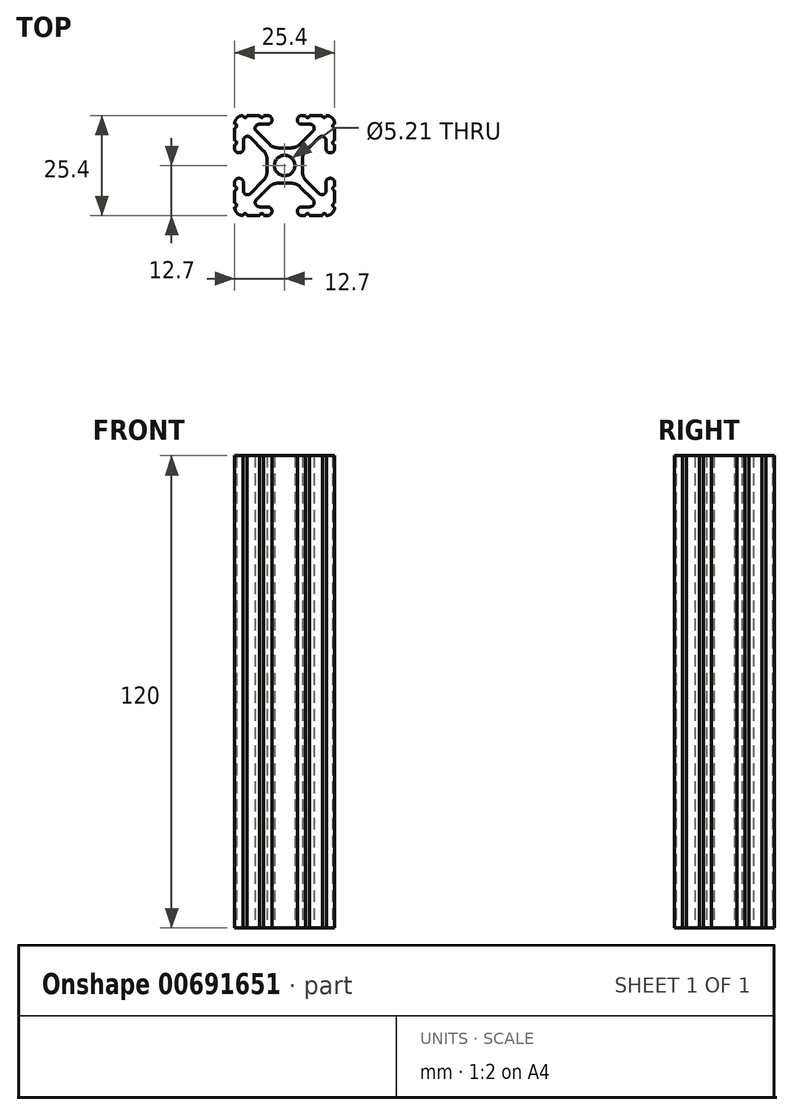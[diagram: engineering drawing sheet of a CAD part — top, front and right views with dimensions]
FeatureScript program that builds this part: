
annotation { "Feature Type Name" : "Feature", "Feature Type Description" : "" }
export const myFeature = defineFeature(function(context is Context, id is Id, definition is map)
    precondition{}
    {
        {
            var Q0;
            Q0=qCreatedBy(makeId("Top.planeOp"),FACE);
            var sketch = newSketch(context, id + "F0", { "sketchPlane" : qUnion([Q0])});
            skCircle(sketch, "E0", {"center": v(0, 0) * mm, "radius": 2.6 * mm});
            skArc(sketch, "E1", {"start": v(-1.7, -4.5) * mm, "mid": v(-2.92, -4.74) * mm, "end": v(-3.95, -5.42) * mm});
            skLineSegment(sketch, "E2", {"start": v(-1.7, -4.5) * mm, "end": v(1.7, -4.5) * mm});
            skArc(sketch, "E3", {"start": v(3.95, -5.42) * mm, "mid": v(2.92, -4.74) * mm, "end": v(1.7, -4.5) * mm});
            skLineSegment(sketch, "E4", {"start": v(3.95, -5.42) * mm, "end": v(7.18, -8.65) * mm});
            skArc(sketch, "E5", {"start": v(6.42, -10.5) * mm, "mid": v(7.41, -9.82) * mm, "end": v(7.18, -8.65) * mm});
            skLineSegment(sketch, "E6", {"start": v(6.42, -10.5) * mm, "end": v(4.29, -10.5) * mm});
            skArc(sketch, "E7", {"start": v(4.29, -10.5) * mm, "mid": v(3.55, -10.8) * mm, "end": v(3.24, -11.54) * mm});
            skLineSegment(sketch, "E8", {"start": v(3.24, -11.54) * mm, "end": v(3.24, -11.65) * mm});
            skArc(sketch, "E9", {"start": v(3.24, -11.65) * mm, "mid": v(3.55, -12.4) * mm, "end": v(4.29, -12.7) * mm});
            skLineSegment(sketch, "E10", {"start": v(4.29, -12.7) * mm, "end": v(5.32, -12.7) * mm});
            skArc(sketch, "E11", {"start": v(6.33, -12.7) * mm, "mid": v(5.83, -12.2) * mm, "end": v(5.32, -12.7) * mm});
            skLineSegment(sketch, "E12", {"start": v(6.33, -12.7) * mm, "end": v(9.55, -12.7) * mm});
            skArc(sketch, "E13", {"start": v(10.57, -12.7) * mm, "mid": v(10.06, -12.2) * mm, "end": v(9.55, -12.7) * mm});
            skArc(sketch, "E14", {"start": v(10.57, -12.7) * mm, "mid": v(12.08, -12.08) * mm, "end": v(12.7, -10.57) * mm});
            skArc(sketch, "E15", {"start": v(12.7, -9.55) * mm, "mid": v(12.2, -10.06) * mm, "end": v(12.7, -10.57) * mm});
            skLineSegment(sketch, "E16", {"start": v(12.7, -9.55) * mm, "end": v(12.7, -6.33) * mm});
            skArc(sketch, "E17", {"start": v(12.7, -5.32) * mm, "mid": v(12.2, -5.83) * mm, "end": v(12.7, -6.33) * mm});
            skLineSegment(sketch, "E18", {"start": v(12.7, -5.32) * mm, "end": v(12.7, -4.29) * mm});
            skArc(sketch, "E19", {"start": v(12.7, -4.29) * mm, "mid": v(12.4, -3.55) * mm, "end": v(11.65, -3.24) * mm});
            skLineSegment(sketch, "E20", {"start": v(11.65, -3.24) * mm, "end": v(11.54, -3.24) * mm});
            skArc(sketch, "E21", {"start": v(11.54, -3.24) * mm, "mid": v(10.8, -3.55) * mm, "end": v(10.5, -4.29) * mm});
            skLineSegment(sketch, "E22", {"start": v(10.5, -4.29) * mm, "end": v(10.5, -6.4) * mm});
            skArc(sketch, "E23", {"start": v(8.74, -7.13) * mm, "mid": v(9.86, -7.35) * mm, "end": v(10.5, -6.4) * mm});
            skLineSegment(sketch, "E24", {"start": v(8.74, -7.13) * mm, "end": v(5.44, -3.84) * mm});
            skArc(sketch, "E25", {"start": v(4.5, -1.6) * mm, "mid": v(4.75, -2.8) * mm, "end": v(5.44, -3.84) * mm});
            skLineSegment(sketch, "E26", {"start": v(4.5, -1.6) * mm, "end": v(4.5, 1.6) * mm});
            skArc(sketch, "E27", {"start": v(5.44, 3.84) * mm, "mid": v(4.75, 2.8) * mm, "end": v(4.5, 1.6) * mm});
            skLineSegment(sketch, "E28", {"start": v(5.44, 3.84) * mm, "end": v(8.74, 7.13) * mm});
            skArc(sketch, "E29", {"start": v(10.5, 6.4) * mm, "mid": v(9.86, 7.35) * mm, "end": v(8.74, 7.13) * mm});
            skLineSegment(sketch, "E30", {"start": v(10.5, 6.4) * mm, "end": v(10.5, 4.29) * mm});
            skArc(sketch, "E31", {"start": v(10.5, 4.29) * mm, "mid": v(10.8, 3.55) * mm, "end": v(11.54, 3.24) * mm});
            skLineSegment(sketch, "E32", {"start": v(11.54, 3.24) * mm, "end": v(11.65, 3.24) * mm});
            skArc(sketch, "E33", {"start": v(11.65, 3.24) * mm, "mid": v(12.4, 3.55) * mm, "end": v(12.7, 4.29) * mm});
            skLineSegment(sketch, "E34", {"start": v(12.7, 4.29) * mm, "end": v(12.7, 5.32) * mm});
            skArc(sketch, "E35", {"start": v(12.7, 6.33) * mm, "mid": v(12.2, 5.83) * mm, "end": v(12.7, 5.32) * mm});
            skLineSegment(sketch, "E36", {"start": v(12.7, 6.33) * mm, "end": v(12.7, 9.55) * mm});
            skArc(sketch, "E37", {"start": v(12.7, 10.57) * mm, "mid": v(12.2, 10.06) * mm, "end": v(12.7, 9.55) * mm});
            skArc(sketch, "E38", {"start": v(12.7, 10.57) * mm, "mid": v(12.08, 12.08) * mm, "end": v(10.57, 12.7) * mm});
            skArc(sketch, "E39", {"start": v(9.55, 12.7) * mm, "mid": v(10.06, 12.2) * mm, "end": v(10.57, 12.7) * mm});
            skLineSegment(sketch, "E40", {"start": v(9.55, 12.7) * mm, "end": v(6.33, 12.7) * mm});
            skArc(sketch, "E41", {"start": v(5.32, 12.7) * mm, "mid": v(5.83, 12.2) * mm, "end": v(6.33, 12.7) * mm});
            skLineSegment(sketch, "E42", {"start": v(5.32, 12.7) * mm, "end": v(4.29, 12.7) * mm});
            skArc(sketch, "E43", {"start": v(4.29, 12.7) * mm, "mid": v(3.55, 12.4) * mm, "end": v(3.24, 11.65) * mm});
            skLineSegment(sketch, "E44", {"start": v(3.24, 11.65) * mm, "end": v(3.24, 11.54) * mm});
            skArc(sketch, "E45", {"start": v(3.24, 11.54) * mm, "mid": v(3.55, 10.8) * mm, "end": v(4.29, 10.5) * mm});
            skLineSegment(sketch, "E46", {"start": v(4.29, 10.5) * mm, "end": v(6.48, 10.5) * mm});
            skArc(sketch, "E47", {"start": v(7.2, 8.72) * mm, "mid": v(7.43, 9.85) * mm, "end": v(6.48, 10.5) * mm});
            skLineSegment(sketch, "E48", {"start": v(7.2, 8.72) * mm, "end": v(3.9, 5.42) * mm});
            skArc(sketch, "E49", {"start": v(1.66, 4.5) * mm, "mid": v(2.87, 4.74) * mm, "end": v(3.9, 5.42) * mm});
            skLineSegment(sketch, "E50", {"start": v(1.66, 4.5) * mm, "end": v(-1.66, 4.5) * mm});
            skArc(sketch, "E51", {"start": v(-3.9, 5.42) * mm, "mid": v(-2.87, 4.74) * mm, "end": v(-1.66, 4.5) * mm});
            skLineSegment(sketch, "E52", {"start": v(-3.9, 5.42) * mm, "end": v(-7.2, 8.72) * mm});
            skArc(sketch, "E53", {"start": v(-6.48, 10.5) * mm, "mid": v(-7.43, 9.85) * mm, "end": v(-7.2, 8.72) * mm});
            skLineSegment(sketch, "E54", {"start": v(-6.48, 10.5) * mm, "end": v(-4.29, 10.5) * mm});
            skArc(sketch, "E55", {"start": v(-4.29, 10.5) * mm, "mid": v(-3.55, 10.8) * mm, "end": v(-3.24, 11.54) * mm});
            skLineSegment(sketch, "E56", {"start": v(-3.24, 11.54) * mm, "end": v(-3.24, 11.65) * mm});
            skArc(sketch, "E57", {"start": v(-3.24, 11.65) * mm, "mid": v(-3.55, 12.4) * mm, "end": v(-4.29, 12.7) * mm});
            skLineSegment(sketch, "E58", {"start": v(-4.29, 12.7) * mm, "end": v(-5.32, 12.7) * mm});
            skArc(sketch, "E59", {"start": v(-6.33, 12.7) * mm, "mid": v(-5.83, 12.2) * mm, "end": v(-5.32, 12.7) * mm});
            skLineSegment(sketch, "E60", {"start": v(-6.33, 12.7) * mm, "end": v(-9.55, 12.7) * mm});
            skArc(sketch, "E61", {"start": v(-10.57, 12.7) * mm, "mid": v(-10.06, 12.2) * mm, "end": v(-9.55, 12.7) * mm});
            skArc(sketch, "E62", {"start": v(-10.57, 12.7) * mm, "mid": v(-12.08, 12.08) * mm, "end": v(-12.7, 10.57) * mm});
            skArc(sketch, "E63", {"start": v(-12.7, 9.55) * mm, "mid": v(-12.2, 10.06) * mm, "end": v(-12.7, 10.57) * mm});
            skLineSegment(sketch, "E64", {"start": v(-12.7, 9.55) * mm, "end": v(-12.7, 6.33) * mm});
            skArc(sketch, "E65", {"start": v(-12.7, 5.32) * mm, "mid": v(-12.2, 5.83) * mm, "end": v(-12.7, 6.33) * mm});
            skLineSegment(sketch, "E66", {"start": v(-12.7, 5.32) * mm, "end": v(-12.7, 4.29) * mm});
            skArc(sketch, "E67", {"start": v(-12.7, 4.29) * mm, "mid": v(-12.4, 3.55) * mm, "end": v(-11.65, 3.24) * mm});
            skLineSegment(sketch, "E68", {"start": v(-11.65, 3.24) * mm, "end": v(-11.54, 3.24) * mm});
            skArc(sketch, "E69", {"start": v(-11.54, 3.24) * mm, "mid": v(-10.8, 3.55) * mm, "end": v(-10.5, 4.29) * mm});
            skLineSegment(sketch, "E70", {"start": v(-10.5, 4.29) * mm, "end": v(-10.5, 6.4) * mm});
            skArc(sketch, "E71", {"start": v(-8.74, 7.13) * mm, "mid": v(-9.86, 7.35) * mm, "end": v(-10.5, 6.4) * mm});
            skLineSegment(sketch, "E72", {"start": v(-8.74, 7.13) * mm, "end": v(-5.44, 3.84) * mm});
            skArc(sketch, "E73", {"start": v(-4.5, 1.6) * mm, "mid": v(-4.75, 2.8) * mm, "end": v(-5.44, 3.84) * mm});
            skLineSegment(sketch, "E74", {"start": v(-4.5, 1.6) * mm, "end": v(-4.5, -1.6) * mm});
            skArc(sketch, "E75", {"start": v(-5.44, -3.84) * mm, "mid": v(-4.75, -2.8) * mm, "end": v(-4.5, -1.6) * mm});
            skLineSegment(sketch, "E76", {"start": v(-5.44, -3.84) * mm, "end": v(-8.74, -7.13) * mm});
            skArc(sketch, "E77", {"start": v(-10.5, -6.4) * mm, "mid": v(-9.86, -7.35) * mm, "end": v(-8.74, -7.13) * mm});
            skLineSegment(sketch, "E78", {"start": v(-10.5, -6.4) * mm, "end": v(-10.5, -4.29) * mm});
            skArc(sketch, "E79", {"start": v(-10.5, -4.29) * mm, "mid": v(-10.8, -3.55) * mm, "end": v(-11.54, -3.24) * mm});
            skLineSegment(sketch, "E80", {"start": v(-11.54, -3.24) * mm, "end": v(-11.65, -3.24) * mm});
            skArc(sketch, "E81", {"start": v(-11.65, -3.24) * mm, "mid": v(-12.4, -3.55) * mm, "end": v(-12.7, -4.29) * mm});
            skLineSegment(sketch, "E82", {"start": v(-12.7, -4.29) * mm, "end": v(-12.7, -5.32) * mm});
            skArc(sketch, "E83", {"start": v(-12.7, -6.33) * mm, "mid": v(-12.2, -5.83) * mm, "end": v(-12.7, -5.32) * mm});
            skLineSegment(sketch, "E84", {"start": v(-12.7, -6.33) * mm, "end": v(-12.7, -9.55) * mm});
            skArc(sketch, "E85", {"start": v(-12.7, -10.57) * mm, "mid": v(-12.2, -10.06) * mm, "end": v(-12.7, -9.55) * mm});
            skArc(sketch, "E86", {"start": v(-12.7, -10.57) * mm, "mid": v(-12.08, -12.08) * mm, "end": v(-10.57, -12.7) * mm});
            skArc(sketch, "E87", {"start": v(-9.55, -12.7) * mm, "mid": v(-10.06, -12.2) * mm, "end": v(-10.57, -12.7) * mm});
            skLineSegment(sketch, "E88", {"start": v(-9.55, -12.7) * mm, "end": v(-6.33, -12.7) * mm});
            skArc(sketch, "E89", {"start": v(-5.32, -12.7) * mm, "mid": v(-5.83, -12.2) * mm, "end": v(-6.33, -12.7) * mm});
            skLineSegment(sketch, "E90", {"start": v(-5.32, -12.7) * mm, "end": v(-4.29, -12.7) * mm});
            skArc(sketch, "E91", {"start": v(-4.29, -12.7) * mm, "mid": v(-3.55, -12.4) * mm, "end": v(-3.24, -11.65) * mm});
            skLineSegment(sketch, "E92", {"start": v(-3.24, -11.65) * mm, "end": v(-3.24, -11.54) * mm});
            skArc(sketch, "E93", {"start": v(-3.24, -11.54) * mm, "mid": v(-3.55, -10.8) * mm, "end": v(-4.29, -10.5) * mm});
            skLineSegment(sketch, "E94", {"start": v(-4.29, -10.5) * mm, "end": v(-6.42, -10.5) * mm});
            skArc(sketch, "E95", {"start": v(-7.18, -8.65) * mm, "mid": v(-7.41, -9.82) * mm, "end": v(-6.42, -10.5) * mm});
            skLineSegment(sketch, "E96", {"start": v(-7.18, -8.65) * mm, "end": v(-3.95, -5.42) * mm});
            skSolve(sketch);
        }
        {
            var Q0;
            Q0=qSketchRegion(id+"F0",true);
            extrude(context, id + "F1", {"entities" : qUnion([Q0]), "depth" : 120 * mm, "offsetDistance" : 25 * mm});
        }
    });
